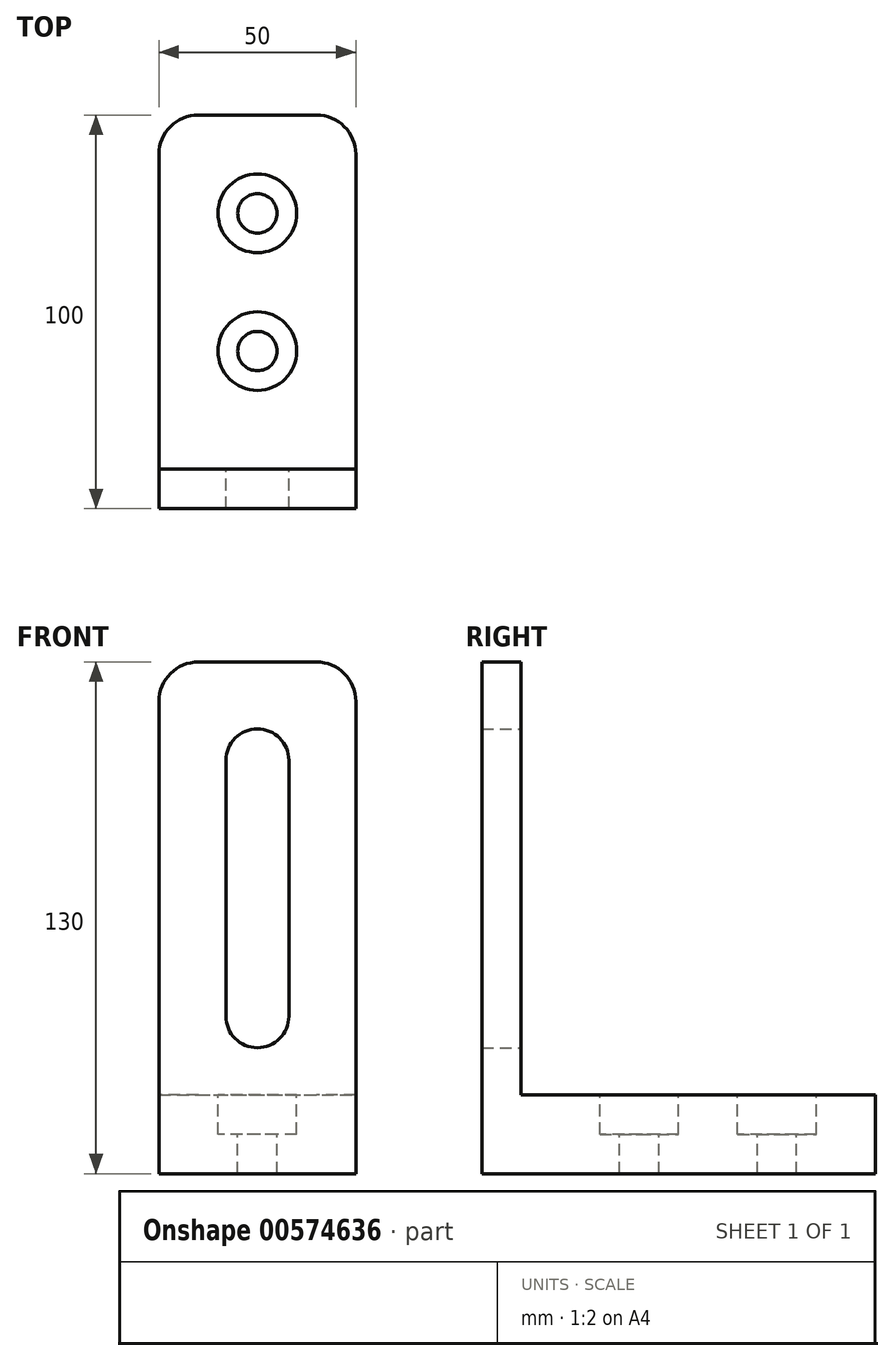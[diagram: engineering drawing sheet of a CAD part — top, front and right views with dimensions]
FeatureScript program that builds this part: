
annotation { "Feature Type Name" : "Feature", "Feature Type Description" : "" }
export const myFeature = defineFeature(function(context is Context, id is Id, definition is map)
    precondition{}
    {
        {
            var Q0;
            Q0=qCreatedBy(makeId("Top.planeOp"),FACE);
            var sketch = newSketch(context, id + "F0", { "sketchPlane" : qUnion([Q0])});
            skLineSegment(sketch, "E0.bottom", {"start": v(0, 0) * mm, "end": v(50, 0) * mm});
            skLineSegment(sketch, "E0.top", {"start": v(0, 100) * mm, "end": v(50, 100) * mm});
            skLineSegment(sketch, "E0.left", {"start": v(0, 0) * mm, "end": v(0, 100) * mm});
            skLineSegment(sketch, "E0.right", {"start": v(50, 0) * mm, "end": v(50, 100) * mm});
            skSolve(sketch);
        }
        {
            var Q0;
            Q0=makeQuery(id+"F0.imprint","IMPRINT",FACE,{"disambiguationData":[TD([[makeQuery(id+"F0.imprint","IMPRINT",EDGE,{"derivedFrom":sQuery(id+"F0.wireOp",EDGE,"E0.bottom")}),1.0]])]});
            extrude(context, id + "F1", {"entities" : qUnion([Q0]), "depth" : 20 * mm, "offsetDistance" : 25 * mm});
        }
        {
            var Q0;
            Q0=makeQuery(id+"F1.opExtrude","CAP_FACE",FACE,{"disambiguationData":[OSD([sQuery(id+"F0.wireOp",EDGE,"E0.bottom"),sQuery(id+"F0.wireOp",EDGE,"E0.top"),sQuery(id+"F0.wireOp",EDGE,"E0.left"),sQuery(id+"F0.wireOp",EDGE,"E0.right")])],"isStart":false});
            var sketch = newSketch(context, id + "F2", { "sketchPlane" : qUnion([Q0])});
            skCircle(sketch, "E1", {"center": v(25, 75) * mm, "radius": 10 * mm});
            skPoint(sketch, "E1.centerSnap0", {"position": v(25, 0) * mm});
            skCircle(sketch, "E2", {"center": v(25, 40) * mm, "radius": 10 * mm});
            skSolve(sketch);
        }
        {
            var Q0;
            Q0=makeQuery(id+"F2.imprint","IMPRINT",FACE,{"disambiguationData":[TD([[makeQuery(id+"F2.imprint","IMPRINT",EDGE,{"derivedFrom":sQuery(id+"F2.wireOp",EDGE,"E1")}),1.0]])]});
            var Q1;
            Q1=makeQuery(id+"F2.imprint","IMPRINT",FACE,{"disambiguationData":[TD([[makeQuery(id+"F2.imprint","IMPRINT",EDGE,{"derivedFrom":sQuery(id+"F2.wireOp",EDGE,"E2")}),1.0]])]});
            extrude(context, id + "F3", {"entities" : qUnion([Q0, Q1]), "operationType" : NewBodyOperationType.REMOVE, "oppositeDirection" : true, "depth" : 10 * mm, "offsetDistance" : 25 * mm});
        }
        {
            var Q0;
            Q0=makeQuery(id+"F3.boolean.opBoolean","COPY",FACE,{"derivedFrom":makeQuery(id+"F3.opExtrude","CAP_FACE",FACE,{"disambiguationData":[OSD([sQuery(id+"F2.wireOp",EDGE,"E1")])],"isStart":false})});
            var sketch = newSketch(context, id + "F4", { "sketchPlane" : qUnion([Q0])});
            skCircle(sketch, "E3", {"center": v(25, 75) * mm, "radius": 5 * mm});
            skSolve(sketch);
        }
        {
            var Q0;
            Q0=makeQuery(id+"F4.imprint","IMPRINT",FACE,{"disambiguationData":[TD([[makeQuery(id+"F4.imprint","IMPRINT",EDGE,{"derivedFrom":sQuery(id+"F4.wireOp",EDGE,"E3")}),1.0]])]});
            extrude(context, id + "F5", {"entities" : qUnion([Q0]), "operationType" : NewBodyOperationType.REMOVE, "oppositeDirection" : true, "depth" : 10 * mm, "offsetDistance" : 25 * mm});
        }
        {
            var Q0;
            Q0=makeQuery(id+"F3.boolean.opBoolean","COPY",FACE,{"derivedFrom":makeQuery(id+"F3.opExtrude","CAP_FACE",FACE,{"disambiguationData":[OSD([sQuery(id+"F2.wireOp",EDGE,"E2")])],"isStart":false})});
            var sketch = newSketch(context, id + "F6", { "sketchPlane" : qUnion([Q0])});
            skCircle(sketch, "E4", {"center": v(25, 40) * mm, "radius": 5 * mm});
            skSolve(sketch);
        }
        {
            var Q0;
            Q0 = qSketchRegion(id + "F6", true);
            extrude(context, id + "F7", {"entities" : qUnion([Q0]), "operationType" : NewBodyOperationType.REMOVE, "oppositeDirection" : true, "depth" : 10 * mm, "offsetDistance" : 25 * mm});
        }
        {
            var Q0;
            Q0=makeQuery(id+"F1.opExtrude","CAP_FACE",FACE,{"disambiguationData":[OSD([sQuery(id+"F0.wireOp",EDGE,"E0.bottom"),sQuery(id+"F0.wireOp",EDGE,"E0.top"),sQuery(id+"F0.wireOp",EDGE,"E0.left"),sQuery(id+"F0.wireOp",EDGE,"E0.right")])],"isStart":false});
            var sketch = newSketch(context, id + "F8", { "sketchPlane" : qUnion([Q0])});
            skLineSegment(sketch, "E5", {"start": v(0, 10) * mm, "end": v(50, 10) * mm});
            skSolve(sketch);
        }
        {
            var Q0;
            Q0 = qSketchRegion(id + "F8", true);
            var Q1;
            {var subQ0=sQuery(id+"F8.wireOp",EDGE,"E5");Q1=makeQuery(id+"F8.imprint","IMPRINT",FACE,{"disambiguationData":[TD([[makeQuery(id+"F8.imprint","IMPRINT",EDGE,{"derivedFrom":subQ0}),-1.0]])]});}
            extrude(context, id + "F9", {"entities" : qUnion([Q0, Q1]), "operationType" : NewBodyOperationType.ADD, "depth" : 110 * mm, "offsetDistance" : 25 * mm});
        }
        {
            var Q0;
            Q0=makeQuery(id+"F1.opExtrude","SWEPT_EDGE",EDGE,{"disambiguationData":[OSD([sQuery(id+"F0.wireOp",EDGE,"E0.top"),sQuery(id+"F0.wireOp",EDGE,"E0.left")])]});
            var Q1;
            Q1=makeQuery(id+"F1.opExtrude","SWEPT_EDGE",EDGE,{"disambiguationData":[OSD([sQuery(id+"F0.wireOp",EDGE,"E0.top"),sQuery(id+"F0.wireOp",EDGE,"E0.right")])]});
            var Q2;
            Q2=makeQuery(id+"F9.opExtrude","CAP_EDGE",EDGE,{"disambiguationData":[OSD([sQuery(id+"F0.wireOp",EDGE,"E0.left")])],"isStart":false});
            var Q3;
            Q3=makeQuery(id+"F9.opExtrude","CAP_EDGE",EDGE,{"disambiguationData":[OSD([sQuery(id+"F0.wireOp",EDGE,"E0.right")])],"isStart":false});
            fillet(context, id + "F10", {"entities" : qUnion([Q0, Q1, Q2, Q3]), "radius" : 10 * mm, "tangentPropagation" : true, "allowEdgeOverflow" : false});
        }
        {
            var Q0;
            Q0=makeQuery(id+"F9.opExtrude","SWEPT_FACE",FACE,{"disambiguationData":[OSD([sQuery(id+"F8.wireOp",EDGE,"E5")])]});
            var sketch = newSketch(context, id + "F11", { "sketchPlane" : qUnion([Q0])});
            skArc(sketch, "E6", {"start": v(-33, 40) * mm, "mid": v(-25, 32) * mm, "end": v(-17, 40) * mm});
            skPoint(sketch, "E6.centerSnap0", {"position": v(-25, 20) * mm});
            skArc(sketch, "E7", {"start": v(-17, 105) * mm, "mid": v(-25, 113) * mm, "end": v(-33, 105) * mm});
            skLineSegment(sketch, "E8", {"start": v(-17, 40) * mm, "end": v(-17, 105) * mm});
            skLineSegment(sketch, "E9", {"start": v(-33, 40) * mm, "end": v(-33, 105) * mm});
            skSolve(sketch);
        }
        {
            var Q0;
            Q0=makeQuery(id+"F11.imprint","IMPRINT",FACE,{"disambiguationData":[TD([[makeQuery(id+"F11.imprint","IMPRINT",EDGE,{"derivedFrom":sQuery(id+"F11.wireOp",EDGE,"E6")}),1.0]])]});
            extrude(context, id + "F12", {"entities" : qUnion([Q0]), "operationType" : NewBodyOperationType.REMOVE, "oppositeDirection" : true, "depth" : 10 * mm, "offsetDistance" : 25 * mm});
        }
    });
